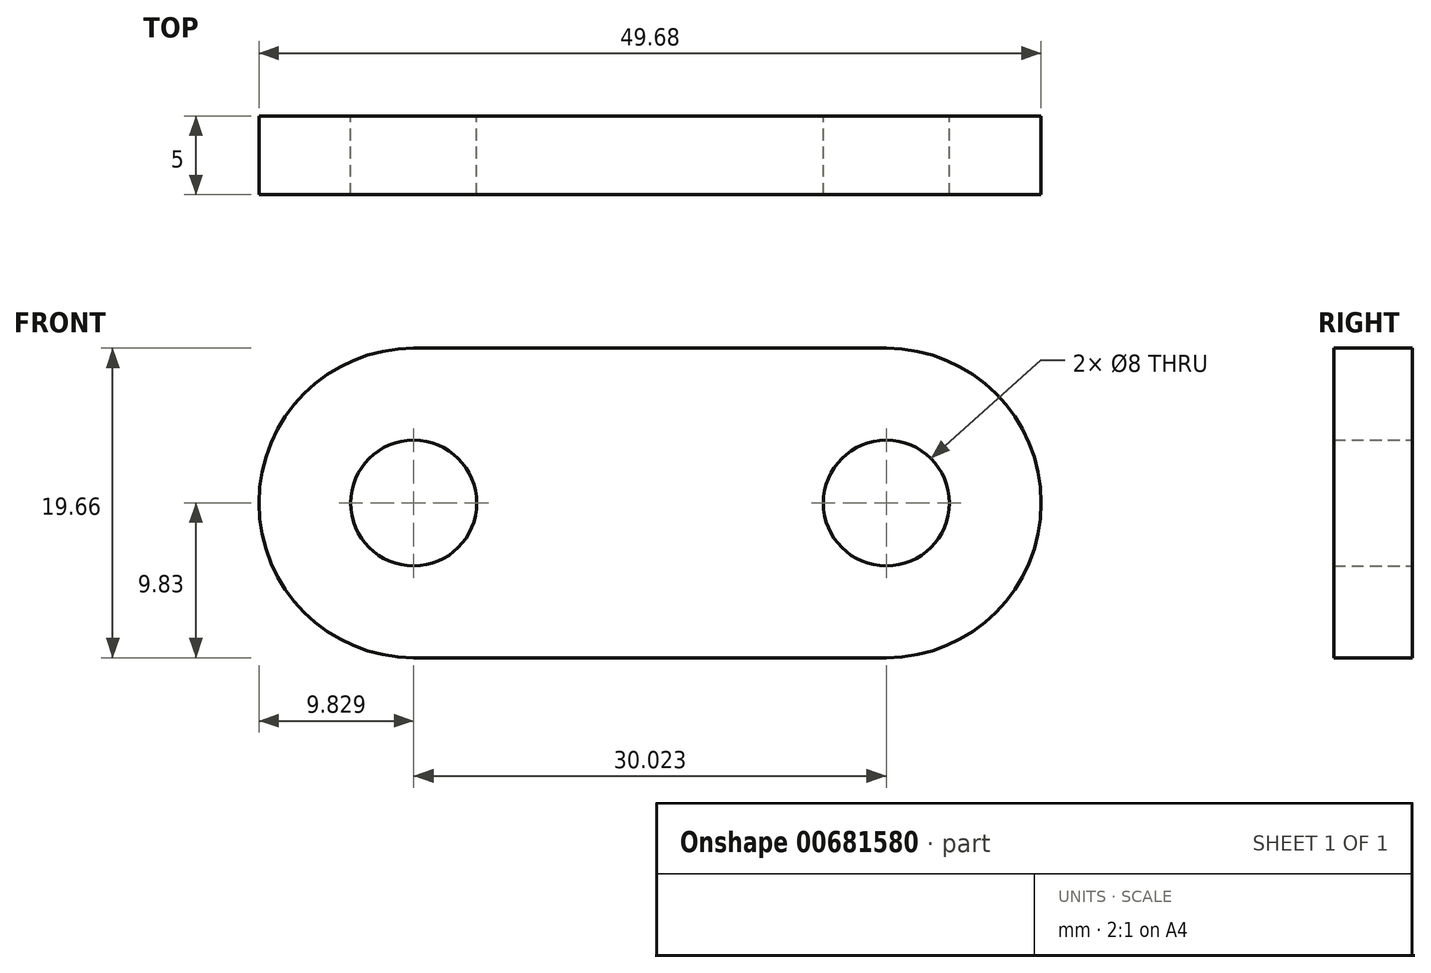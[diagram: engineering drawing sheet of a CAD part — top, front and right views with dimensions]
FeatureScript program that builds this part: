
annotation { "Feature Type Name" : "Feature", "Feature Type Description" : "" }
export const myFeature = defineFeature(function(context is Context, id is Id, definition is map)
    precondition{}
    {
        {
            var Q0;
            Q0=qCreatedBy(makeId("Front.planeOp"),FACE);
            var sketch = newSketch(context, id + "F0", { "sketchPlane" : qUnion([Q0])});
            skLineSegment(sketch, "E0", {"start": v(0, 0) * mm, "end": v(-24.84, 0) * mm});
            skArc(sketch, "E1", {"start": v(-15.01, 9.83) * mm, "mid": v(-24.84, 0) * mm, "end": v(-15.01, -9.83) * mm});
            skLineSegment(sketch, "E2", {"start": v(0, 9.83) * mm, "end": v(-15.01, 9.83) * mm});
            skLineSegment(sketch, "E3.MirrorCS", {"start": v(0, -9.83) * mm, "end": v(-15.01, -9.83) * mm});
            skPoint(sketch, "E4.orphan", {"position": v(-36.16, -9.83) * mm});
            skPoint(sketch, "E5.orphan", {"position": v(-36.16, 9.83) * mm});
            skLineSegment(sketch, "E6", {"start": v(0, 0) * mm, "end": v(0, 32.1) * mm});
            skLineSegment(sketch, "E7.MirrorCS", {"start": v(0, 9.83) * mm, "end": v(15.01, 9.83) * mm});
            skLineSegment(sketch, "E8.MirrorCS", {"start": v(0, -9.83) * mm, "end": v(15.01, -9.83) * mm});
            skArc(sketch, "E9.MirrorCS", {"start": v(15.01, 9.83) * mm, "mid": v(24.84, 0) * mm, "end": v(15.01, -9.83) * mm});
            skCircle(sketch, "E10", {"center": v(-15.01, 0) * mm, "radius": 4 * mm});
            skCircle(sketch, "E11.MirrorC", {"center": v(15.01, 0) * mm, "radius": 4 * mm});
            skSolve(sketch);
        }
        {
            var Q0;
            {var subQ0=sQuery(id+"F0.wireOp",EDGE,"E3.MirrorCS");Q0=makeQuery(id+"F0.imprint","IMPRINT",FACE,{"disambiguationData":[TD([[makeQuery(id+"F0.imprint","IMPRINT",EDGE,{"derivedFrom":subQ0}),-1.0]])]});}
            var Q1;
            {var subQ3=sQuery(id+"F0.wireOp",EDGE,"E2");Q1=makeQuery(id+"F0.imprint","IMPRINT",FACE,{"disambiguationData":[TD([[makeQuery(id+"F0.imprint","IMPRINT",EDGE,{"derivedFrom":subQ3}),1.0]])]});}
            extrude(context, id + "F1", {"entities" : qUnion([Q0, Q1]), "endBound" : BoundingType.SYMMETRIC, "depth" : 5 * mm, "offsetDistance" : 25.4 * mm});
        }
    });
